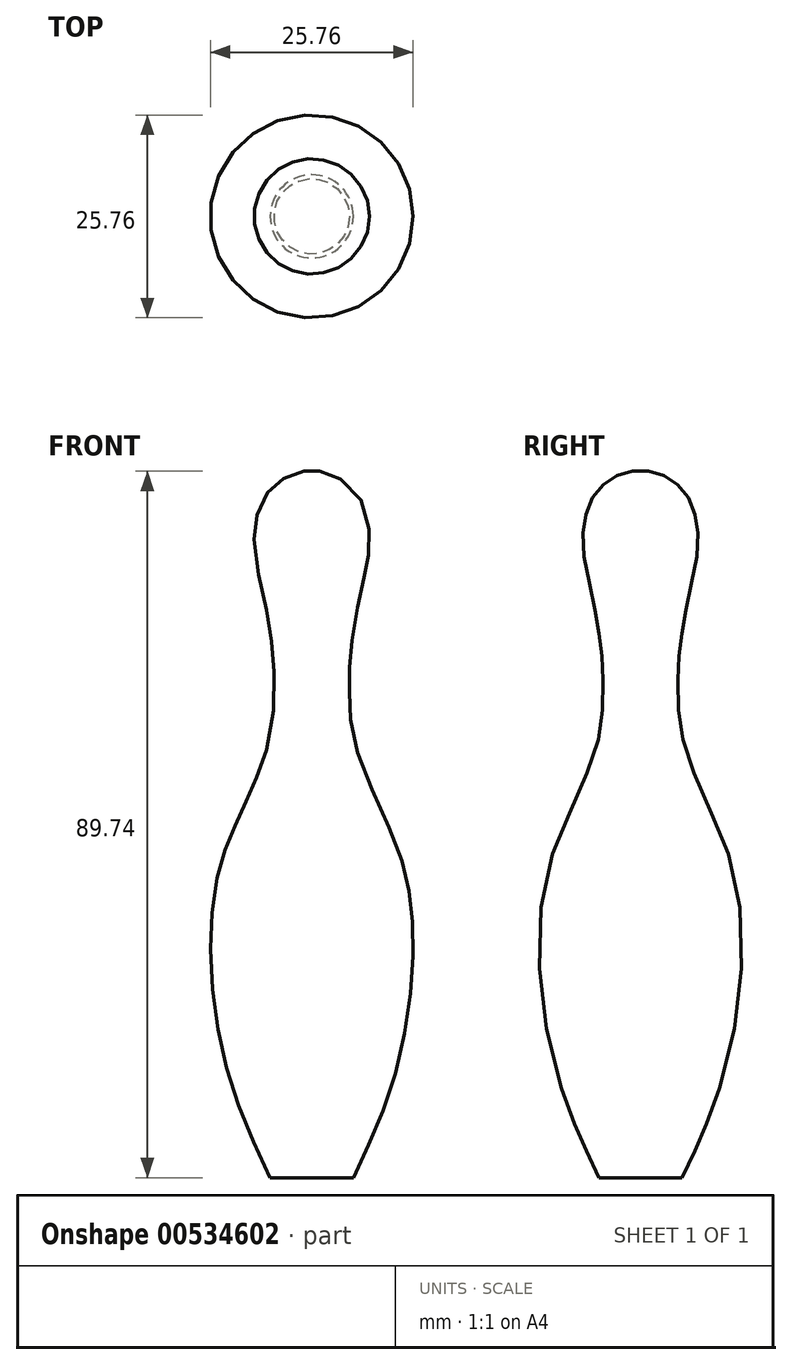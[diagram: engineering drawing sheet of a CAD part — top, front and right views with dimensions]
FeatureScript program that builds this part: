
annotation { "Feature Type Name" : "Feature", "Feature Type Description" : "" }
export const myFeature = defineFeature(function(context is Context, id is Id, definition is map)
    precondition{}
    {
        {
            var Q0;
            Q0=qCreatedBy(makeId("Front.planeOp"),FACE);
            var sketch = newSketch(context, id + "F0", { "sketchPlane" : qUnion([Q0])});
            skLineSegment(sketch, "E0", {"start": v(14, 35.77) * mm, "end": v(14, 0) * mm, "construction": true});
            skLineSegment(sketch, "E1", {"start": v(0, 0) * mm, "end": v(5.29, 0) * mm});
            skLineSegment(sketch, "E2", {"start": v(0, 89.74) * mm, "end": v(0, 0) * mm});
            skFitSpline(sketch, "E3", {"points": [v(1, 89.74) * mm, v(5.51, 87.23) * mm, v(7.32, 80.47) * mm, v(6.57, 75.86) * mm, v(5, 67.4) * mm, v(4.79, 62.06) * mm, v(5.62, 54.63) * mm, v(10.78, 42.26) * mm, v(12.63, 34.19) * mm, v(12.63, 23.93) * mm, v(9.79, 10.57) * mm, v(5.29, 0) * mm], "startDerivative": vector(40.92, 0) * mm, "endDerivative": vector(-45.36, -94.74) * mm});
            skLineSegment(sketch, "E4", {"start": v(1, 89.74) * mm, "end": v(0, 89.74) * mm});
            skPoint(sketch, "E5.orphan", {"position": v(0, 91.3) * mm});
            skSolve(sketch);
        }
        {
            var Q0;
            Q0=makeQuery(id+"F0.imprint","IMPRINT",FACE,{"disambiguationData":[TD([[makeQuery(id+"F0.imprint","IMPRINT",EDGE,{"derivedFrom":sQuery(id+"F0.wireOp",EDGE,"E1")}),1.0]])]});
            var Q1;
            Q1=sQuery(id+"F0.wireOp",EDGE,"E2");
            revolve(context, id + "F1", {"entities" : qUnion([Q0]), "axis" : qUnion([Q1]), "revolveType" : RevolveType.FULL});
        }
    });
